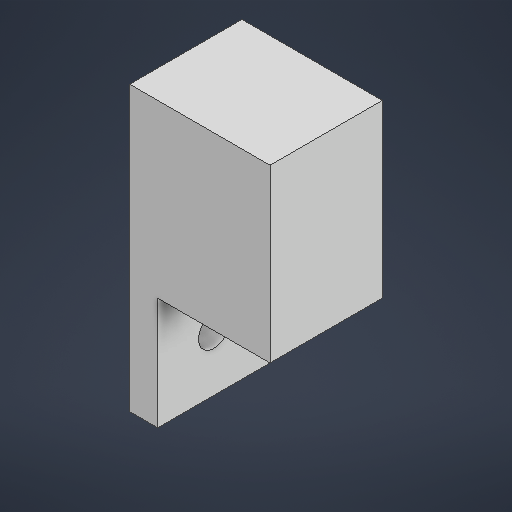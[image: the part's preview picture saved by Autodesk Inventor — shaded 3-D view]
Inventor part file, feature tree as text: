
AUTODESK INVENTOR PART (.ipt)
format: ipt  version: 2025 (Build 290162000, 162)  size: 192,000 bytes
history: native  units: in
note: dims shown in document units (in); Inventor stores cm internally (conversion verified against a paired STEP export)
features: extrude x3, sketch x3
ambient origin geometry x8: Origin, YZ Plane, XZ Plane, XY Plane, X Axis, Y Axis, Z Axis, Center Point
bodies: Solid1 (feature_tree)
feature tree (6):
  extrude  "Extrusion1"  Depth=0.9843in
  extrude  "Extrusion2"  Depth=0.1575in
  extrude  "Extrusion3"  Depth=0.7874in
  sketch  "Sketch1"  dims[d0=0.9449in d1=0.9843in]
  sketch  "Sketch2"  dims[d2=90.0deg d3=0.1575in]
  sketch  "Sketch3"  dims[d4=90.0deg d5=0.7874in d6=0.7874in d7=0.0in d8=0.2165in d9=0.7874in d10=0.0in d11=1.0433in d12=0.0in]
